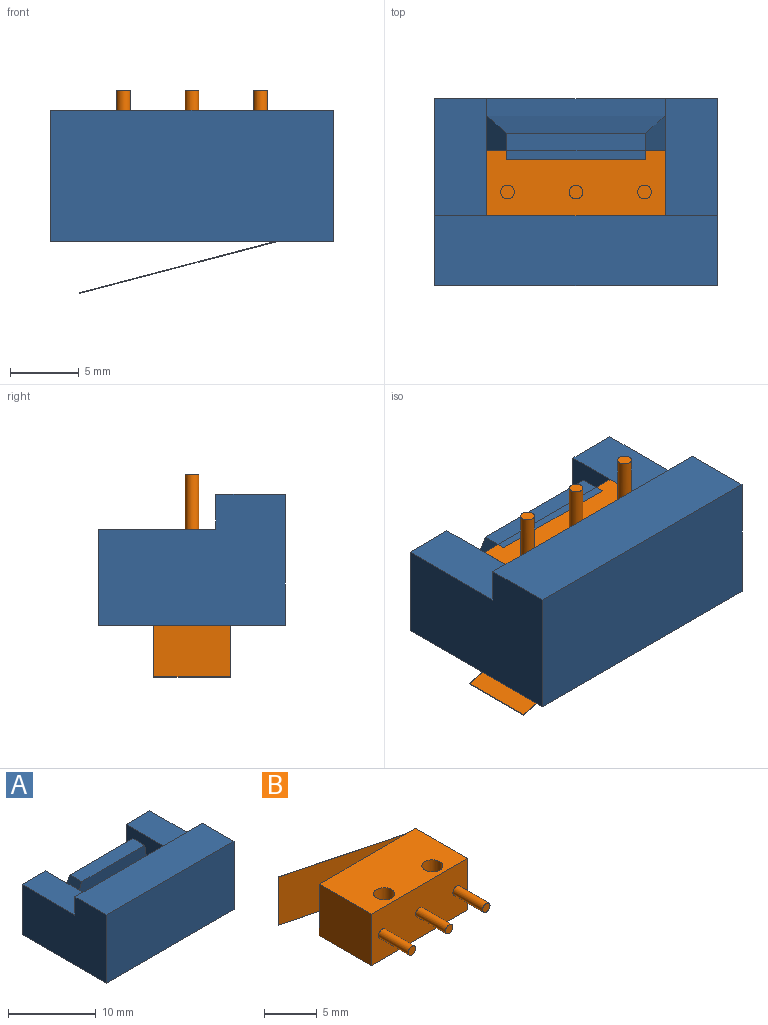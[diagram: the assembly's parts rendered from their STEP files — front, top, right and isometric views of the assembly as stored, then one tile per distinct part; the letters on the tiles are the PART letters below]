
ASSEMBLY  parts=2 mates=1
PART A: 20 faces, bbox 20.6x13.6x9.6 mm
  f0: plane 13.01x1.27mm, normal (0,0,1), area 16.5mm2, adj f3,f4,f9,f17
  f1: plane 8.56x3.81mm, normal (0,0,1), area 32.6mm2, adj f3,f4,f8,f13
  f2: plane 13.01x1.27mm, normal (0,-1,0), area 16.5mm2, adj f4,f9,f11,f19
  f3: plane 20.62x7.01mm, normal (0,1,0), area 69.9mm2, adj f0,f1,f4,f6,f8,f9,f10,f11
  f4: plane 9.83x7.01mm, normal (-1,0,0), area 64.1mm2, adj f0,f1,f2,f3,f5,f11,f12,f16
  f5: plane 13.01x7.01mm, normal (0,1,0), area 91.2mm2, adj f4,f9,f11,f12
  f6: plane 13.64x9.55mm, normal (-1,0,0), area 108.5mm2, adj f3,f7,f10,f11,f13,f14
  f7: plane 20.62x9.55mm, normal (0,-1,0), area 197mm2, adj f6,f8,f11,f14
  f8: plane 13.64x9.55mm, normal (1,0,0), area 108.5mm2, adj f1,f3,f7,f11,f13,f14
  f9: plane 9.83x7.01mm, normal (1,0,0), area 64.1mm2, adj f0,f2,f3,f5,f10,f11,f12,f18
  f10: plane 8.56x3.81mm, normal (0,0,1), area 32.6mm2, adj f3,f6,f9,f13
  f11: plane 20.62x13.64mm, normal (0,0,-1), area 203mm2, adj f2,f3,f4,f5,f6,f7,f8,f9
  f12: plane 13.01x1.27mm, normal (0,0,-1), area 16.5mm2, adj f4,f5,f9,f13
  f13: plane 20.62x2.54mm, normal (0,1,0), area 52.4mm2, adj f1,f6,f8,f10,f12,f14
  f14: plane 20.62x5.08mm, normal (0,0,1), area 104.8mm2, adj f6,f7,f8,f13
  f15: plane 10.16x1.91mm, normal (0,0,1), area 19.4mm2, adj f16,f17,f18,f19
  f16: plane 5.74x3.18mm, normal (0.97,0,0.24), area 13.1mm2, adj f4,f15,f17,f19
  f17: plane 13.01x5.74mm, normal (0,0.98,0.22), area 68.1mm2, adj f0,f15,f16,f18
  f18: plane 5.74x3.18mm, normal (-0.97,0,0.24), area 13.1mm2, adj f9,f15,f17,f19
  f19: plane 13.01x5.74mm, normal (0,-0.99,-0.11), area 66.9mm2, adj f2,f15,f16,f18
PART B: 19 faces, bbox 14.7x14.8x6 mm
  f0: plane 5.6x0.05mm, normal (-1,0,0), area 0.3mm2, adj f1,f2,f17,f18
  f1: plane 14.51x5.6mm, normal (0.25,0.97,0), area 84mm2, adj f0,f3,f17,f18
  f2: plane 14.31x5.6mm, normal (-0.25,-0.97,0), area 82.8mm2, adj f0,f3,f17,f18
  f3: plane 13x6mm, normal (0,1,0), area 76.9mm2, adj f1,f2,f4,f6,f7,f8,f17,f18
  f4: plane 7x6mm, normal (-1,0,0), area 42mm2, adj f3,f5,f7,f8
  f5: plane 13x6mm, normal (0,-1,0), area 75.6mm2, adj f4,f6,f7,f8,f11,f13,f15
  f6: plane 7x6mm, normal (1,0,0), area 42mm2, adj f3,f5,f7,f8
  f7: plane 13x7mm, normal (0,0,1), area 84.7mm2, adj f3,f4,f5,f6,f9,f10
  f8: plane 13x7mm, normal (0,0,-1), area 84.7mm2, adj f3,f4,f5,f6,f9,f10
  f9: cylinder r=1mm len=6mm, axis (0,0,1), area 37.7mm2, adj f7,f8
  f10: cylinder r=1mm len=6mm, axis (0,0,1), area 37.7mm2, adj f7,f8
  f11: cylinder r=0.5mm len=4mm, axis (0,1,0), area 12.6mm2, adj f5,f12
  f12: plane 1x1mm, normal (0,-1,0), area 0.8mm2, adj f11
  f13: cylinder r=0.5mm len=4mm, axis (0,1,0), area 12.6mm2, adj f5,f14
  f14: plane 1x1mm, normal (0,-1,0), area 0.8mm2, adj f13
  f15: cylinder r=0.5mm len=4mm, axis (0,1,0), area 12.6mm2, adj f5,f16
  f16: plane 1x1mm, normal (0,-1,0), area 0.8mm2, adj f15
  f17: plane 14.51x3.81mm, normal (0,0,1), area 0.8mm2, adj f0,f1,f2,f3
  f18: plane 14.51x3.81mm, normal (0,0,-1), area 0.8mm2, adj f0,f1,f2,f3
PLACE A at identity fixed
PLACE B rot(axis=(-1,0,0),90deg) t=(-7.94,-3.01,17.9)mm
MATE fastened B.f8 <-> A.f5  axis (0,-1,0) through (0,-3.01,0)mm
